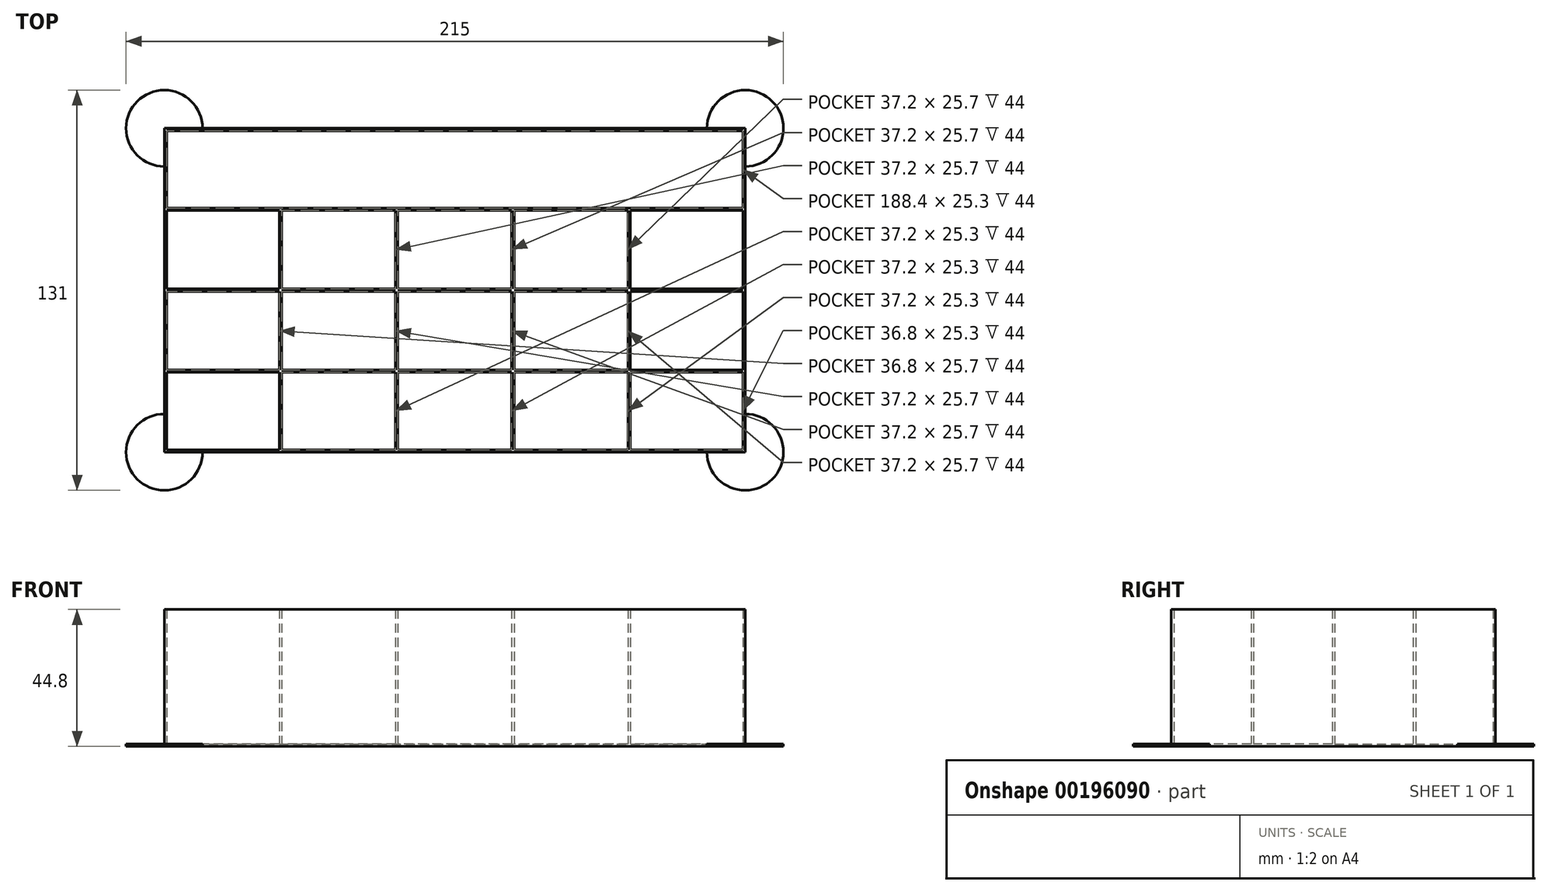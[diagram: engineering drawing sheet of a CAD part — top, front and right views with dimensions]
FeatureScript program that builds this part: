
annotation { "Feature Type Name" : "Feature", "Feature Type Description" : "" }
export const myFeature = defineFeature(function(context is Context, id is Id, definition is map)
    precondition{}
    {
        {
            var Q0;
            Q0=qCreatedBy(makeId("Top.planeOp"),FACE);
            var sketch = newSketch(context, id + "F0", { "sketchPlane" : qUnion([Q0])});
            skLineSegment(sketch, "E0.bottom", {"start": v(0, 0) * mm, "end": v(-190, 0) * mm});
            skLineSegment(sketch, "E0.top", {"start": v(0, 106) * mm, "end": v(-190, 106) * mm});
            skLineSegment(sketch, "E0.left", {"start": v(0, 0) * mm, "end": v(0, 106) * mm});
            skLineSegment(sketch, "E0.right", {"start": v(-190, 0) * mm, "end": v(-190, 106) * mm});
            skSolve(sketch);
        }
        {
            var Q0;
            Q0=makeQuery(id+"F0.imprint","IMPRINT",FACE,{"disambiguationData":[TD([[makeQuery(id+"F0.imprint","IMPRINT",EDGE,{"derivedFrom":sQuery(id+"F0.wireOp",EDGE,"2yAqHf39-Fc5o-gFfP-nSkp-kWoTTWPsp9CE.bottom")}),-1.0]])]});
            var Q1;
            Q1=makeQuery(id+"F0.imprint","IMPRINT",FACE,{"disambiguationData":[TD([[makeQuery(id+"F0.imprint","IMPRINT",EDGE,{"derivedFrom":sQuery(id+"F0.wireOp",EDGE,"E0.bottom")}),-1.0]])]});
            extrude(context, id + "F1", {"entities" : qUnion([Q0, Q1]), "depth" : 0.8 * mm});
        }
        {
            var Q0;
            Q0=makeQuery(id+"F1.opExtrude","CAP_FACE",FACE,{"disambiguationData":[OSD([sQuery(id+"F0.wireOp",EDGE,"E0.bottom"),sQuery(id+"F0.wireOp",EDGE,"E0.top"),sQuery(id+"F0.wireOp",EDGE,"E0.left"),sQuery(id+"F0.wireOp",EDGE,"E0.right"),sQuery(id+"F0.wireOp",EDGE,"2yAqHf39-Fc5o-gFfP-nSkp-kWoTTWPsp9CE.top"),sQuery(id+"F0.wireOp",EDGE,"2yAqHf39-Fc5o-gFfP-nSkp-kWoTTWPsp9CE.left"),sQuery(id+"F0.wireOp",EDGE,"2yAqHf39-Fc5o-gFfP-nSkp-kWoTTWPsp9CE.right")])],"isStart":false});
            var sketch = newSketch(context, id + "F2", { "sketchPlane" : qUnion([Q0])});
            skLineSegment(sketch, "E1.0", {"start": v(-190, 0) * mm, "end": v(-190, 106) * mm});
            skLineSegment(sketch, "E1.1", {"start": v(0, 106) * mm, "end": v(-190, 106) * mm});
            skLineSegment(sketch, "E1.5", {"start": v(0, 0) * mm, "end": v(-190, 0) * mm});
            skLineSegment(sketch, "E2", {"start": v(-190, 53) * mm, "end": v(0, 53) * mm, "construction": true});
            skLineSegment(sketch, "E3", {"start": v(-190, 106) * mm, "end": v(0, 106) * mm, "construction": true});
            skLineSegment(sketch, "E4", {"start": v(-190, 26.5) * mm, "end": v(0, 26.5) * mm, "construction": true});
            skLineSegment(sketch, "E5", {"start": v(-190, 79.5) * mm, "end": v(0, 79.5) * mm, "construction": true});
            skLineSegment(sketch, "E6", {"start": v(-152, 0) * mm, "end": v(-152, 106) * mm, "construction": true});
            skLineSegment(sketch, "E7", {"start": v(-114, 106) * mm, "end": v(-114, 0) * mm, "construction": true});
            skLineSegment(sketch, "E8", {"start": v(-76, 106) * mm, "end": v(-76, 0) * mm, "construction": true});
            skLineSegment(sketch, "E9", {"start": v(-38, 106) * mm, "end": v(-38, 0) * mm, "construction": true});
            skLineSegment(sketch, "E10.bottom", {"start": v(-0.8, 52.6) * mm, "end": v(-37.6, 52.6) * mm});
            skLineSegment(sketch, "E10.top", {"start": v(-0.8, 26.9) * mm, "end": v(-37.6, 26.9) * mm});
            skLineSegment(sketch, "E10.left", {"start": v(-0.8, 52.6) * mm, "end": v(-0.8, 26.9) * mm});
            skLineSegment(sketch, "E10.right", {"start": v(-37.6, 52.6) * mm, "end": v(-37.6, 26.9) * mm});
            skLineSegment(sketch, "E11.bottom", {"start": v(-38.4, 52.6) * mm, "end": v(-75.6, 52.6) * mm});
            skLineSegment(sketch, "E11.top", {"start": v(-38.4, 26.9) * mm, "end": v(-75.6, 26.9) * mm});
            skLineSegment(sketch, "E11.left", {"start": v(-38.4, 52.6) * mm, "end": v(-38.4, 26.9) * mm});
            skLineSegment(sketch, "E11.right", {"start": v(-75.6, 52.6) * mm, "end": v(-75.6, 26.9) * mm});
            skLineSegment(sketch, "E12.bottom", {"start": v(-76.4, 52.6) * mm, "end": v(-113.6, 52.6) * mm});
            skLineSegment(sketch, "E12.top", {"start": v(-76.4, 26.9) * mm, "end": v(-113.6, 26.9) * mm});
            skLineSegment(sketch, "E12.left", {"start": v(-76.4, 52.6) * mm, "end": v(-76.4, 26.9) * mm});
            skLineSegment(sketch, "E12.right", {"start": v(-113.6, 52.6) * mm, "end": v(-113.6, 26.9) * mm});
            skLineSegment(sketch, "E13.bottom", {"start": v(-114.4, 52.6) * mm, "end": v(-151.6, 52.6) * mm});
            skLineSegment(sketch, "E13.top", {"start": v(-114.4, 26.9) * mm, "end": v(-151.6, 26.9) * mm});
            skLineSegment(sketch, "E13.left", {"start": v(-114.4, 52.6) * mm, "end": v(-114.4, 26.9) * mm});
            skLineSegment(sketch, "E13.right", {"start": v(-151.6, 52.6) * mm, "end": v(-151.6, 26.9) * mm});
            skLineSegment(sketch, "E14.bottom", {"start": v(-152.4, 52.6) * mm, "end": v(-189.2, 52.6) * mm});
            skLineSegment(sketch, "E14.top", {"start": v(-152.4, 26.9) * mm, "end": v(-189.2, 26.9) * mm});
            skLineSegment(sketch, "E14.left", {"start": v(-152.4, 52.6) * mm, "end": v(-152.4, 26.9) * mm});
            skLineSegment(sketch, "E14.right", {"start": v(-189.2, 52.6) * mm, "end": v(-189.2, 26.9) * mm});
            skLineSegment(sketch, "E15.bottom", {"start": v(-0.8, 26.1) * mm, "end": v(-37.6, 26.1) * mm});
            skLineSegment(sketch, "E15.top", {"start": v(-0.8, 0.8) * mm, "end": v(-37.6, 0.8) * mm});
            skLineSegment(sketch, "E15.left", {"start": v(-0.8, 26.1) * mm, "end": v(-0.8, 0.8) * mm});
            skLineSegment(sketch, "E15.right", {"start": v(-37.6, 26.1) * mm, "end": v(-37.6, 0.8) * mm});
            skLineSegment(sketch, "E16.bottom", {"start": v(-38.4, 26.1) * mm, "end": v(-75.6, 26.1) * mm});
            skLineSegment(sketch, "E16.top", {"start": v(-38.4, 0.8) * mm, "end": v(-75.6, 0.8) * mm});
            skLineSegment(sketch, "E16.left", {"start": v(-38.4, 26.1) * mm, "end": v(-38.4, 0.8) * mm});
            skLineSegment(sketch, "E16.right", {"start": v(-75.6, 26.1) * mm, "end": v(-75.6, 0.8) * mm});
            skLineSegment(sketch, "E17.bottom", {"start": v(-76.4, 26.1) * mm, "end": v(-113.6, 26.1) * mm});
            skLineSegment(sketch, "E17.top", {"start": v(-76.4, 0.8) * mm, "end": v(-113.6, 0.8) * mm});
            skLineSegment(sketch, "E17.left", {"start": v(-76.4, 26.1) * mm, "end": v(-76.4, 0.8) * mm});
            skLineSegment(sketch, "E17.right", {"start": v(-113.6, 26.1) * mm, "end": v(-113.6, 0.8) * mm});
            skLineSegment(sketch, "E18.bottom", {"start": v(-114.4, 26.1) * mm, "end": v(-151.6, 26.1) * mm});
            skLineSegment(sketch, "E18.top", {"start": v(-114.4, 0.8) * mm, "end": v(-151.6, 0.8) * mm});
            skLineSegment(sketch, "E18.left", {"start": v(-114.4, 26.1) * mm, "end": v(-114.4, 0.8) * mm});
            skLineSegment(sketch, "E18.right", {"start": v(-151.6, 26.1) * mm, "end": v(-151.6, 0.8) * mm});
            skLineSegment(sketch, "E19.bottom", {"start": v(-152.4, 26.1) * mm, "end": v(-189.2, 26.1) * mm});
            skLineSegment(sketch, "E19.top", {"start": v(-152.4, 0.8) * mm, "end": v(-189.2, 0.8) * mm});
            skLineSegment(sketch, "E19.left", {"start": v(-152.4, 26.1) * mm, "end": v(-152.4, 0.8) * mm});
            skLineSegment(sketch, "E19.right", {"start": v(-189.2, 26.1) * mm, "end": v(-189.2, 0.8) * mm});
            skLineSegment(sketch, "E20.bottom", {"start": v(-0.8, 53.4) * mm, "end": v(-37.6, 53.4) * mm});
            skLineSegment(sketch, "E20.top", {"start": v(-0.8, 79.1) * mm, "end": v(-37.6, 79.1) * mm});
            skLineSegment(sketch, "E20.left", {"start": v(-0.8, 53.4) * mm, "end": v(-0.8, 79.1) * mm});
            skLineSegment(sketch, "E20.right", {"start": v(-37.6, 53.4) * mm, "end": v(-37.6, 79.1) * mm});
            skLineSegment(sketch, "E21.bottom", {"start": v(-38.4, 53.4) * mm, "end": v(-75.6, 53.4) * mm});
            skLineSegment(sketch, "E21.top", {"start": v(-38.4, 79.1) * mm, "end": v(-75.6, 79.1) * mm});
            skLineSegment(sketch, "E21.left", {"start": v(-38.4, 53.4) * mm, "end": v(-38.4, 79.1) * mm});
            skLineSegment(sketch, "E21.right", {"start": v(-75.6, 53.4) * mm, "end": v(-75.6, 79.1) * mm});
            skLineSegment(sketch, "E22.bottom", {"start": v(-76.4, 53.4) * mm, "end": v(-113.6, 53.4) * mm});
            skLineSegment(sketch, "E22.top", {"start": v(-76.4, 79.1) * mm, "end": v(-113.6, 79.1) * mm});
            skLineSegment(sketch, "E22.left", {"start": v(-76.4, 53.4) * mm, "end": v(-76.4, 79.1) * mm});
            skLineSegment(sketch, "E22.right", {"start": v(-113.6, 53.4) * mm, "end": v(-113.6, 79.1) * mm});
            skLineSegment(sketch, "E23.bottom", {"start": v(-114.4, 53.4) * mm, "end": v(-151.6, 53.4) * mm});
            skLineSegment(sketch, "E23.top", {"start": v(-114.4, 79.1) * mm, "end": v(-151.6, 79.1) * mm});
            skLineSegment(sketch, "E23.left", {"start": v(-114.4, 53.4) * mm, "end": v(-114.4, 79.1) * mm});
            skLineSegment(sketch, "E23.right", {"start": v(-151.6, 53.4) * mm, "end": v(-151.6, 79.1) * mm});
            skLineSegment(sketch, "E24.bottom", {"start": v(-152.4, 53.4) * mm, "end": v(-189.2, 53.4) * mm});
            skLineSegment(sketch, "E24.top", {"start": v(-152.4, 79.1) * mm, "end": v(-189.2, 79.1) * mm});
            skLineSegment(sketch, "E24.left", {"start": v(-152.4, 53.4) * mm, "end": v(-152.4, 79.1) * mm});
            skLineSegment(sketch, "E24.right", {"start": v(-189.2, 53.4) * mm, "end": v(-189.2, 79.1) * mm});
            skLineSegment(sketch, "E25.bottom", {"start": v(-189.2, 79.9) * mm, "end": v(-0.8, 79.9) * mm});
            skLineSegment(sketch, "E25.top", {"start": v(-189.2, 105.2) * mm, "end": v(-0.8, 105.2) * mm});
            skLineSegment(sketch, "E25.left", {"start": v(-189.2, 79.9) * mm, "end": v(-189.2, 105.2) * mm});
            skLineSegment(sketch, "E25.right", {"start": v(-0.8, 79.9) * mm, "end": v(-0.8, 105.2) * mm});
            skSolve(sketch);
        }
        {
            var Q0;
            Q0=makeQuery(id+"F2.imprint","IMPRINT",FACE,{"disambiguationData":[TD([[makeQuery(id+"F2.imprint","IMPRINT",EDGE,{"derivedFrom":sQuery(id+"F2.wireOp",EDGE,"E1.0")}),-1.0]])]});
            extrude(context, id + "F3", {"entities" : qUnion([Q0]), "operationType" : NewBodyOperationType.ADD, "depth" : 44 * mm});
        }
        {
            var Q0;
            Q0=makeQuery(id+"F1.opExtrude","CAP_FACE",FACE,{"disambiguationData":[OSD([sQuery(id+"F0.wireOp",EDGE,"E0.bottom"),sQuery(id+"F0.wireOp",EDGE,"E0.top"),sQuery(id+"F0.wireOp",EDGE,"E0.left"),sQuery(id+"F0.wireOp",EDGE,"E0.right"),sQuery(id+"F0.wireOp",EDGE,"2yAqHf39-Fc5o-gFfP-nSkp-kWoTTWPsp9CE.top"),sQuery(id+"F0.wireOp",EDGE,"2yAqHf39-Fc5o-gFfP-nSkp-kWoTTWPsp9CE.left"),sQuery(id+"F0.wireOp",EDGE,"2yAqHf39-Fc5o-gFfP-nSkp-kWoTTWPsp9CE.right")])],"isStart":true});
            var sketch = newSketch(context, id + "F4", { "sketchPlane" : qUnion([Q0])});
            skCircle(sketch, "E26", {"center": v(0, 0) * mm, "radius": 12.5 * mm});
            skCircle(sketch, "E27", {"center": v(-190, 0) * mm, "radius": 12.5 * mm});
            skCircle(sketch, "E28", {"center": v(-190, -106) * mm, "radius": 12.5 * mm});
            skCircle(sketch, "E29", {"center": v(0, -106) * mm, "radius": 12.5 * mm});
            skSolve(sketch);
        }
        {
            var Q0;
            Q0=qSketchRegion(id+"F4",true);
            extrude(context, id + "F5", {"entities" : qUnion([Q0]), "operationType" : NewBodyOperationType.ADD, "oppositeDirection" : true, "depth" : 0.8 * mm});
        }
    });
